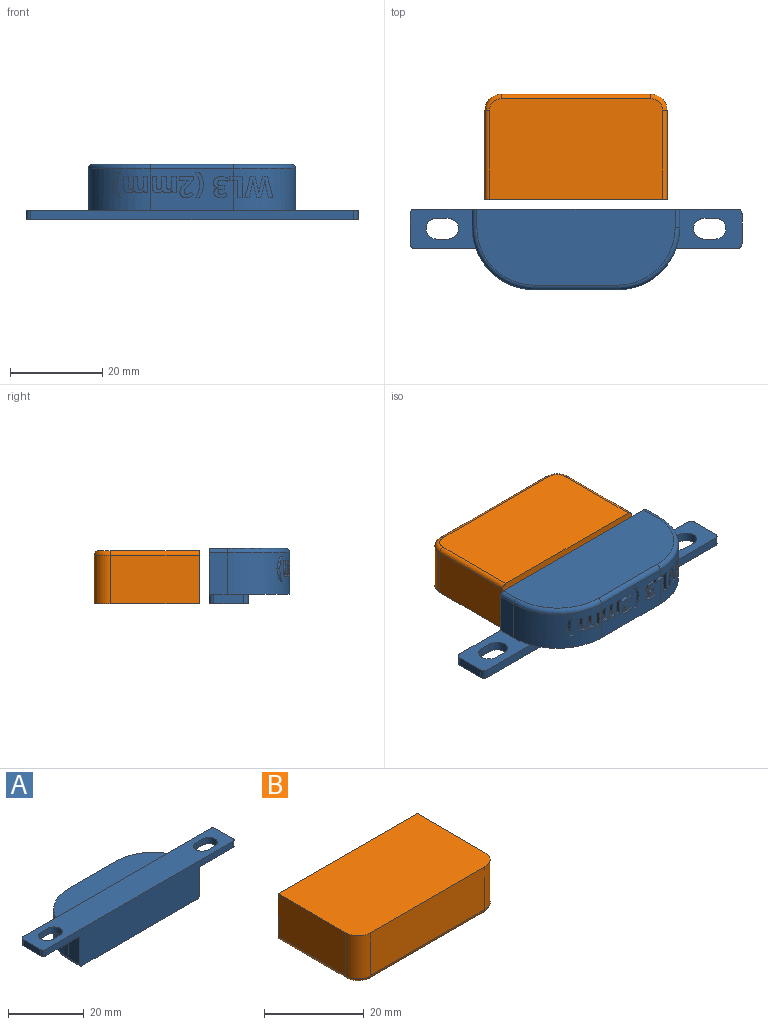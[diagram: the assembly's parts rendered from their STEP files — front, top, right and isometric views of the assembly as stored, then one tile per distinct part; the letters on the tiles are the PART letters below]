
ASSEMBLY  parts=2 mates=1
PART A: 197 faces, bbox 72.1x18.7x12.1 mm
  f0: cylinder r=13.5mm len=13.5mm, axis (0,0,1), area 174mm2, adj f1,f13,f14,f16,f153,f154,f155,f156
  f1: plane 18x9mm, normal (0,1,0), area 130.8mm2, adj f0,f2,f16,f28,f29,f30,f60,f61
  f2: cylinder r=13.5mm len=13.5mm, axis (0,0,1), area 170.5mm2, adj f1,f16,f24,f25,f28,f30,f31,f32
  f3: plane 2.5x2mm, normal (0,1,0), area 5mm2, adj f4,f11,f12,f13
  f4: cylinder r=2.25mm len=4.5mm, axis (0,0,-1), area 14.1mm2, adj f3,f5,f12,f13
  f5: plane 2.5x2mm, normal (0,-1,0), area 5mm2, adj f4,f11,f12,f13
  f6: plane 70x12mm, normal (0,-1,0), area 589.6mm2, adj f10,f12,f13,f14,f15,f22,f24,f25
  f7: plane 70x2mm, normal (0,1,0), area 140mm2, adj f8,f12,f13,f16,f20,f24
  f8: cylinder r=1mm len=2mm, axis (0,0,-1), area 3.1mm2, adj f7,f9,f12,f13
  f9: plane 6.5x2mm, normal (-1,0,0), area 13mm2, adj f8,f10,f12,f13
  f10: cylinder r=1mm len=2mm, axis (0,0,-1), area 3.1mm2, adj f6,f9,f12,f13
  f11: cylinder r=2.25mm len=4.5mm, axis (0,0,-1), area 14.1mm2, adj f3,f5,f12,f13
  f12: plane 72x8.5mm, normal (0,0,1), area 556.8mm2, adj f3,f4,f5,f6,f7,f8,f9,f10
  f13: plane 14.27x8.5mm, normal (0,0,-1), area 88.3mm2, adj f0,f3,f4,f5,f6,f7,f8,f9
  f14: plane 9x4mm, normal (-1,0,0), area 36mm2, adj f0,f6,f13,f192
  f15: plane 43x16.5mm, normal (0,0,-1), area 642.4mm2, adj f6,f192,f193,f194,f195,f196
  f16: plane 43.46x9mm, normal (0,0,1), area 329.1mm2, adj f0,f1,f2,f7
  f17: plane 2.5x2mm, normal (0,1,0), area 5mm2, adj f12,f18,f23,f24
  f18: cylinder r=2.25mm len=4.5mm, axis (0,0,-1), area 14.1mm2, adj f12,f17,f19,f24
  f19: plane 2.5x2mm, normal (0,-1,0), area 5mm2, adj f12,f18,f23,f24
  f20: cylinder r=1mm len=2mm, axis (0,0,-1), area 3.1mm2, adj f7,f12,f21,f24
  f21: plane 6.5x2mm, normal (1,0,0), area 13mm2, adj f12,f20,f22,f24
  f22: cylinder r=1mm len=2mm, axis (0,0,-1), area 3.1mm2, adj f6,f12,f21,f24
  f23: cylinder r=2.25mm len=4.5mm, axis (0,0,-1), area 14.1mm2, adj f12,f17,f19,f24
  f24: plane 14.27x8.5mm, normal (0,0,-1), area 88.3mm2, adj f2,f6,f7,f17,f18,f19,f20,f21
  f25: plane 9x4mm, normal (1,0,0), area 36mm2, adj f2,f6,f24,f196
  f26: cylinder r=13.5mm len=4.47mm, axis (0,0,1), area 5mm2, adj f27,f28,f30,f31,f32,f33
  f27: plane 0.85x0.78mm, normal (0,1,0), area 0.7mm2, adj f26,f28,f29,f30
  f28: plane 2.76x1.14mm, normal (0,0,1), area 2.8mm2, adj f1,f2,f26,f27,f29,f31
  f29: plane 1x0.78mm, normal (1,0,0), area 0.8mm2, adj f1,f27,f28,f30
  f30: plane 1.81x1.03mm, normal (0,0,-1), area 1.8mm2, adj f1,f2,f26,f27,f29,f32
  f31: plane 4.47x1mm, normal (-1,0,0), area 4.5mm2, adj f2,f26,f28,f33
  f32: plane 3.69x1mm, normal (1,0,0), area 3.7mm2, adj f2,f26,f30,f33
  f33: plane 1.1x0.95mm, normal (0,0,-1), area 0.9mm2, adj f2,f26,f31,f32
  f34: cylinder r=13.5mm len=6.05mm, axis (0,0,1), area 15.4mm2, adj f35,f36,f37,f38,f39,f40,f41,f42
  f35: plane 4.49x1.29mm, normal (0.97,0,0.25), area 4.6mm2, adj f2,f34,f36,f56
  f36: plane 1.21x0.93mm, normal (0,0,-1), area 0.9mm2, adj f2,f34,f35,f37
  f37: plane 2.45x1.17mm, normal (-0.97,0,-0.23), area 2.5mm2, adj f2,f34,f36,f38
  f38: extruded ~1.04x0.58mm, area 0.6mm2, adj f2,f34,f37,f39
  f39: extruded ~1.03x0.6mm, area 0.6mm2, adj f2,f34,f38,f40
  f40: extruded ~1.03x0.59mm, area 0.6mm2, adj f2,f34,f39,f41
  f41: extruded ~1.04x0.51mm, area 0.5mm2, adj f2,f34,f40,f42
  f42: plane 2.52x1.26mm, normal (0.97,0,-0.25), area 2.6mm2, adj f2,f34,f41,f43
  f43: plane 1.4x0.9mm, normal (0,0,-1), area 0.9mm2, adj f2,f34,f42,f44
  f44: plane 2.52x1.36mm, normal (-0.97,0,-0.25), area 2.6mm2, adj f2,f34,f43,f45
  f45: extruded ~1.07x0.57mm, area 0.6mm2, adj f2,f34,f44,f46
  f46: extruded ~1.05x0.54mm, area 0.5mm2, adj f2,f34,f45,f47
  f47: extruded ~1.17x1.13mm, area 1.2mm2, adj f2,f34,f46,f48
  f48: plane 2.46x1.39mm, normal (0.97,0,-0.23), area 2.5mm2, adj f2,f34,f47,f49
  f49: plane 1.7x0.93mm, normal (0,0,-1), area 0.9mm2, adj f2,f34,f48,f50
  f50: plane 4.56x1.92mm, normal (-0.97,0,0.25), area 4.6mm2, adj f2,f34,f49,f51
  f51: plane 1.64x1.08mm, normal (0,0,1), area 1.1mm2, adj f2,f34,f50,f52
  f52: plane 2.36x1.31mm, normal (0.97,0,0.25), area 2.4mm2, adj f2,f34,f51,f53
  f53: extruded ~1.05x0.52mm, area 0.5mm2, adj f2,f34,f52,f54
  f54: extruded ~1.04x0.53mm, area 0.5mm2, adj f2,f34,f53,f55
  f55: extruded ~1.04x0.53mm, area 0.5mm2, adj f2,f34,f54,f57
  f56: plane 1.35x1.08mm, normal (0,0,1), area 1.1mm2, adj f2,f34,f35,f58
  f57: extruded ~1.05x0.52mm, area 0.5mm2, adj f2,f34,f55,f58
  f58: plane 2.36x1.25mm, normal (-0.97,0,0.25), area 2.4mm2, adj f2,f34,f56,f57
  f59: plane 5.19x3.48mm, normal (0,1,0), area 11.1mm2, adj f60,f61,f62,f63,f64,f65,f66,f67
  f60: plane 1.72x1mm, normal (1,0,0), area 1.7mm2, adj f1,f59,f61,f85
  f61: extruded ~1x0.78mm, area 0.8mm2, adj f1,f59,f60,f62
  f62: extruded ~1x0.51mm, area 0.6mm2, adj f1,f59,f61,f63
  f63: extruded ~1x0.39mm, area 0.5mm2, adj f1,f59,f62,f64
  f64: extruded ~1x0.55mm, area 0.6mm2, adj f1,f59,f63,f65
  f65: plane 2x1mm, normal (-1,0,0), area 2mm2, adj f1,f59,f64,f66
  f66: plane 1x0.94mm, normal (0,0,1), area 0.9mm2, adj f1,f59,f65,f67
  f67: plane 2.23x1mm, normal (1,0,0), area 2.2mm2, adj f1,f59,f66,f68
  f68: extruded ~1x0.96mm, area 1mm2, adj f1,f59,f67,f69
  f69: extruded ~1x0.88mm, area 1mm2, adj f1,f59,f68,f70
  f70: extruded ~1x0.6mm, area 0.6mm2, adj f1,f59,f69,f71
  f71: extruded ~1x0.41mm, area 0.6mm2, adj f1,f59,f70,f72
  f72: plane 1x0.08mm, normal (0,0,-1), area 0.1mm2, adj f1,f59,f71,f73
  f73: extruded ~1.04x1mm, area 1.2mm2, adj f1,f59,f72,f74
  f74: extruded ~1x0.6mm, area 0.6mm2, adj f1,f59,f73,f75
  f75: extruded ~1x0.4mm, area 0.5mm2, adj f1,f59,f74,f76
  f76: plane 1x0.05mm, normal (0,0,-1), area 0.1mm2, adj f1,f59,f75,f77
  f77: plane 1x0.44mm, normal (0.96,0,-0.28), area 0.5mm2, adj f1,f59,f76,f78
  f78: plane 1x0.71mm, normal (0,0,-1), area 0.7mm2, adj f1,f59,f77,f79
  f79: plane 3.42x1mm, normal (-1,0,0), area 3.4mm2, adj f1,f59,f78,f80
  f80: plane 1x0.93mm, normal (0,0,1), area 0.9mm2, adj f1,f59,f79,f81
  f81: plane 1.61x1mm, normal (1,0,0), area 1.6mm2, adj f1,f59,f80,f82
  f82: extruded ~1x0.87mm, area 0.9mm2, adj f1,f59,f81,f83
  f83: extruded ~1x0.52mm, area 0.6mm2, adj f1,f59,f82,f84
  f84: extruded ~1x0.39mm, area 0.5mm2, adj f1,f59,f83,f86
  f85: plane 1x0.93mm, normal (0,0,1), area 0.9mm2, adj f1,f59,f60,f87
  f86: extruded ~1x0.55mm, area 0.6mm2, adj f1,f59,f84,f87
  f87: plane 2x1mm, normal (-1,0,0), area 2mm2, adj f1,f59,f85,f86
  f88: plane 4.53x3.14mm, normal (0,1,0), area 7.4mm2, adj f89,f90,f91,f92,f93,f94,f95,f96
  f89: plane 1x0.8mm, normal (1,0,0), area 0.8mm2, adj f1,f88,f90,f110
  f90: plane 1.95x1mm, normal (0,0,-1), area 1.9mm2, adj f1,f88,f89,f91
  f91: plane 1x0.04mm, normal (1,0,0), area 0mm2, adj f1,f88,f90,f92
  f92: plane 1x0.58mm, normal (0.69,0,0.73), area 0.8mm2, adj f1,f88,f91,f93
  f93: extruded ~1x0.81mm, area 1.1mm2, adj f1,f88,f92,f94
  f94: extruded ~1x0.55mm, area 0.7mm2, adj f1,f88,f93,f95
  f95: extruded ~1x0.58mm, area 0.6mm2, adj f1,f88,f94,f96
  f96: extruded ~1x0.63mm, area 0.7mm2, adj f1,f88,f95,f97
  f97: extruded ~1x0.5mm, area 0.7mm2, adj f1,f88,f96,f98
  f98: extruded ~1x0.74mm, area 0.8mm2, adj f1,f88,f97,f99
  f99: extruded ~1x0.58mm, area 0.6mm2, adj f1,f88,f98,f100
  f100: extruded ~1x0.47mm, area 0.5mm2, adj f1,f88,f99,f101
  f101: extruded ~1x0.55mm, area 0.7mm2, adj f1,f88,f100,f102
  f102: plane 1x0.61mm, normal (-0.76,0,0.65), area 0.8mm2, adj f1,f88,f101,f103
  f103: extruded ~1x0.51mm, area 0.6mm2, adj f1,f88,f102,f104
  f104: extruded ~1x0.5mm, area 0.5mm2, adj f1,f88,f103,f105
  f105: extruded ~1x0.4mm, area 0.4mm2, adj f1,f88,f104,f106
  f106: extruded ~1x0.4mm, area 0.4mm2, adj f1,f88,f105,f107
  f107: extruded ~1x0.35mm, area 0.4mm2, adj f1,f88,f106,f108
  f108: extruded ~1x0.37mm, area 0.4mm2, adj f1,f88,f107,f109
  f109: extruded ~1x0.71mm, area 1mm2, adj f1,f88,f108,f111
  f110: plane 3.13x1mm, normal (0,0,1), area 3.1mm2, adj f1,f88,f89,f112
  f111: plane 1.13x1.12mm, normal (-0.71,0,-0.7), area 1.6mm2, adj f1,f88,f109,f112
  f112: plane 1x0.66mm, normal (-1,0,0), area 0.7mm2, adj f1,f88,f110,f111
  f113: plane 5.46x1.69mm, normal (0,1,0), area 4.4mm2, adj f114,f115,f116,f117,f118,f119,f120,f121
  f114: extruded ~1.49x1mm, area 1.5mm2, adj f1,f113,f115,f121
  f115: extruded ~1.21x1mm, area 1.4mm2, adj f1,f113,f114,f116
  f116: plane 1x0.76mm, normal (0,0,1), area 0.8mm2, adj f1,f113,f115,f117
  f117: extruded ~1.27x1mm, area 1.4mm2, adj f1,f113,f116,f118
  f118: extruded ~1.45x1mm, area 1.5mm2, adj f1,f113,f117,f119
  f119: extruded ~1.45x1mm, area 1.5mm2, adj f1,f113,f118,f120
  f120: extruded ~1.3x1mm, area 1.5mm2, adj f1,f113,f119,f122
  f121: extruded ~1.52x1mm, area 1.5mm2, adj f1,f113,f114,f123
  f122: plane 1x0.76mm, normal (0,0,-1), area 0.8mm2, adj f1,f113,f120,f123
  f123: extruded ~1.24x1mm, area 1.4mm2, adj f1,f113,f121,f122
  f124: plane 4.6x3.09mm, normal (0,1,0), area 7.6mm2, adj f125,f126,f127,f128,f129,f130,f131,f132
  f125: extruded ~1x0.78mm, area 0.9mm2, adj f1,f124,f126,f149
  f126: extruded ~1.1x1mm, area 1.1mm2, adj f1,f124,f125,f127
  f127: extruded ~1.46x1mm, area 1.5mm2, adj f1,f124,f126,f128
  f128: plane 1x0.65mm, normal (-0.83,0,0.56), area 0.8mm2, adj f1,f124,f127,f129
  f129: extruded ~1x0.51mm, area 0.6mm2, adj f1,f124,f128,f130
  f130: extruded ~1x0.45mm, area 0.5mm2, adj f1,f124,f129,f131
  f131: extruded ~1x0.64mm, area 0.9mm2, adj f1,f124,f130,f132
  f132: extruded ~1x0.47mm, area 0.6mm2, adj f1,f124,f131,f133
  f133: extruded ~1x0.76mm, area 0.8mm2, adj f1,f124,f132,f134
  f134: plane 1x0.35mm, normal (0,0,-1), area 0.3mm2, adj f1,f124,f133,f135
  f135: plane 1x0.73mm, normal (-1,0,0), area 0.7mm2, adj f1,f124,f134,f136
  f136: plane 1x0.34mm, normal (0,0,1), area 0.3mm2, adj f1,f124,f135,f137
  f137: extruded ~1x0.82mm, area 0.8mm2, adj f1,f124,f136,f138
  f138: extruded ~1x0.45mm, area 0.5mm2, adj f1,f124,f137,f139
  f139: extruded ~1x0.51mm, area 0.6mm2, adj f1,f124,f138,f140
  f140: extruded ~1x0.69mm, area 0.7mm2, adj f1,f124,f139,f141
  f141: extruded ~1x0.62mm, area 0.6mm2, adj f1,f124,f140,f142
  f142: extruded ~1x0.57mm, area 0.6mm2, adj f1,f124,f141,f143
  f143: plane 1x0.8mm, normal (-1,0,0), area 0.8mm2, adj f1,f124,f142,f144
  f144: extruded ~1.29x1mm, area 1.3mm2, adj f1,f124,f143,f145
  f145: extruded ~1.34x1mm, area 1.4mm2, adj f1,f124,f144,f146
  f146: extruded ~1x1mm, area 1.2mm2, adj f1,f124,f145,f147
  f147: extruded ~1x0.71mm, area 0.8mm2, adj f1,f124,f146,f148
  f148: extruded ~1x0.82mm, area 0.9mm2, adj f1,f124,f147,f150
  f149: extruded ~1x0.71mm, area 0.8mm2, adj f1,f124,f125,f151
  f150: plane 1x0.02mm, normal (1,0,0), area 0mm2, adj f1,f124,f148,f151
  f151: extruded ~1x0.71mm, area 0.8mm2, adj f1,f124,f149,f150
  f152: cylinder r=13.5mm len=5.46mm, axis (0,0,1), area 5.3mm2, adj f153,f154,f155,f156,f157,f158,f159,f160
  f153: extruded ~1.51x1.17mm, area 1.5mm2, adj f0,f152,f154,f160
  f154: extruded ~1.46x1.24mm, area 1.4mm2, adj f0,f152,f153,f155
  f155: plane 1.45x0.76mm, normal (0,0,-1), area 0.8mm2, adj f0,f152,f154,f156
  f156: extruded ~1.38x1.3mm, area 1.5mm2, adj f0,f152,f155,f157
  f157: extruded ~1.45x1.14mm, area 1.5mm2, adj f0,f152,f156,f158
  f158: extruded ~1.45x1.14mm, area 1.5mm2, adj f0,f152,f157,f159
  f159: extruded ~1.37x1.26mm, area 1.4mm2, adj f0,f152,f158,f161
  f160: extruded ~1.5x1.18mm, area 1.5mm2, adj f0,f152,f153,f162
  f161: plane 1.45x0.76mm, normal (0,0,1), area 0.8mm2, adj f0,f152,f159,f162
  f162: extruded ~1.46x1.21mm, area 1.4mm2, adj f0,f152,f160,f161
  f163: cylinder r=13.5mm len=5.19mm, axis (0,0,1), area 11.5mm2, adj f164,f165,f166,f167,f168,f169,f170,f171
  f164: plane 1.72x1mm, normal (1,0,0), area 1.7mm2, adj f0,f163,f165,f189
  f165: extruded ~1.05x0.78mm, area 0.8mm2, adj f0,f163,f164,f166
  f166: extruded ~1.16x0.51mm, area 0.6mm2, adj f0,f163,f165,f167
  f167: extruded ~1.14x0.39mm, area 0.5mm2, adj f0,f163,f166,f168
  f168: extruded ~1.05x0.55mm, area 0.6mm2, adj f0,f163,f167,f169
  f169: plane 2x1mm, normal (-1,0,0), area 2mm2, adj f0,f163,f168,f170
  f170: plane 1.4x0.94mm, normal (0,0,1), area 0.9mm2, adj f0,f163,f169,f171
  f171: plane 2.23x1mm, normal (1,0,0), area 2.2mm2, adj f0,f163,f170,f172
  f172: extruded ~1.14x0.96mm, area 1mm2, adj f0,f163,f171,f173
  f173: extruded ~1.36x0.88mm, area 1mm2, adj f0,f163,f172,f174
  f174: extruded ~1.2x0.6mm, area 0.6mm2, adj f0,f163,f173,f175
  f175: extruded ~1.12x0.41mm, area 0.6mm2, adj f0,f163,f174,f176
  f176: plane 1.02x0.08mm, normal (0,0,-1), area 0.1mm2, adj f0,f163,f175,f177
  f177: extruded ~1.24x1.04mm, area 1.2mm2, adj f0,f163,f176,f178
  f178: extruded ~1.1x0.6mm, area 0.6mm2, adj f0,f163,f177,f179
  f179: extruded ~1.05x0.4mm, area 0.5mm2, adj f0,f163,f178,f180
  f180: plane 1.01x0.05mm, normal (0,0,-1), area 0.1mm2, adj f0,f163,f179,f181
  f181: plane 1.01x0.44mm, normal (0.96,0,-0.28), area 0.5mm2, adj f0,f163,f180,f182
  f182: plane 1.05x0.71mm, normal (0,0,-1), area 0.7mm2, adj f0,f163,f181,f183
  f183: plane 3.42x1mm, normal (-1,0,0), area 3.4mm2, adj f0,f163,f182,f184
  f184: plane 1.07x0.93mm, normal (0,0,1), area 0.9mm2, adj f0,f163,f183,f185
  f185: plane 1.61x1mm, normal (1,0,0), area 1.6mm2, adj f0,f163,f184,f186
  f186: extruded ~1.02x0.87mm, area 0.9mm2, adj f0,f163,f185,f187
  f187: extruded ~1.08x0.52mm, area 0.6mm2, adj f0,f163,f186,f188
  f188: extruded ~1.07x0.39mm, area 0.5mm2, adj f0,f163,f187,f190
  f189: plane 1.23x0.93mm, normal (0,0,1), area 0.9mm2, adj f0,f163,f164,f191
  f190: extruded ~1.03x0.55mm, area 0.6mm2, adj f0,f163,f188,f191
  f191: plane 2x1mm, normal (-1,0,0), area 2mm2, adj f0,f163,f189,f190
  f192: cylinder r=1mm len=4mm, axis (0,1,0), area 6.3mm2, adj f6,f14,f15,f193
  f193: torus R=12.5mm, axis (0,0,1), area 32.4mm2, adj f0,f15,f192,f194
  f194: cylinder r=1mm len=18mm, axis (1,0,0), area 28.3mm2, adj f1,f15,f193,f195
  f195: torus R=12.5mm, axis (0,0,1), area 32.4mm2, adj f2,f15,f194,f196
  f196: cylinder r=1mm len=4mm, axis (0,1,0), area 6.3mm2, adj f6,f15,f25,f195
PART B: 178 faces, bbox 40.1x23.1x11.5 mm
  f0: plane 39.5x11.5mm, normal (0,1,0), area 388.3mm2, adj f2,f4,f5,f6,f8,f9,f10,f11
  f1: plane 32.5x10.5mm, normal (0,-1,0), area 341.3mm2, adj f3,f5,f7,f175
  f2: plane 19.3x10.5mm, normal (-1,0,0), area 202.7mm2, adj f0,f3,f5,f173
  f3: cylinder r=3.5mm len=10.5mm, axis (0,0,1), area 57.7mm2, adj f1,f2,f5,f174
  f4: plane 37.5x21.8mm, normal (0,0,-1), area 814.8mm2, adj f0,f173,f174,f175,f176,f177
  f5: plane 39.5x22.8mm, normal (0,0,1), area 895.3mm2, adj f0,f1,f2,f3,f6,f7
  f6: plane 19.3x10.5mm, normal (1,0,0), area 202.7mm2, adj f0,f5,f7,f177
  f7: cylinder r=3.5mm len=10.5mm, axis (0,0,1), area 57.7mm2, adj f1,f5,f6,f176
  f8: extruded ~1.5x1mm, area 1.5mm2, adj f0,f9,f17,f18
  f9: extruded ~1.51x1mm, area 1.5mm2, adj f0,f8,f10,f18
  f10: extruded ~1.24x1mm, area 1.4mm2, adj f0,f9,f11,f18
  f11: plane 1x0.76mm, normal (0,0,-1), area 0.8mm2, adj f0,f10,f12,f18
  f12: extruded ~1.3x1mm, area 1.5mm2, adj f0,f11,f13,f18
  f13: extruded ~1.45x1mm, area 1.5mm2, adj f0,f12,f14,f18
  f14: extruded ~1.45x1mm, area 1.5mm2, adj f0,f13,f15,f18
  f15: extruded ~1.26x1mm, area 1.4mm2, adj f0,f14,f16,f18
  f16: plane 1x0.76mm, normal (0,0,1), area 0.8mm2, adj f0,f15,f17,f18
  f17: extruded ~1.21x1mm, area 1.4mm2, adj f0,f8,f16,f18
  f18: plane 5.46x1.69mm, normal (0,1,0), area 4.4mm2, adj f8,f9,f10,f11,f12,f13,f14,f15
  f19: plane 1x0.93mm, normal (0,0,1), area 0.9mm2, adj f0,f20,f46,f47
  f20: plane 1.72x1mm, normal (1,0,0), area 1.7mm2, adj f0,f19,f21,f47
  f21: extruded ~1x0.78mm, area 0.8mm2, adj f0,f20,f22,f47
  f22: extruded ~1x0.51mm, area 0.6mm2, adj f0,f21,f23,f47
  f23: extruded ~1x0.39mm, area 0.5mm2, adj f0,f22,f24,f47
  f24: extruded ~1x0.55mm, area 0.6mm2, adj f0,f23,f25,f47
  f25: plane 2x1mm, normal (-1,0,0), area 2mm2, adj f0,f24,f26,f47
  f26: plane 1x0.94mm, normal (0,0,1), area 0.9mm2, adj f0,f25,f27,f47
  f27: plane 2.23x1mm, normal (1,0,0), area 2.2mm2, adj f0,f26,f28,f47
  f28: extruded ~1x0.96mm, area 1mm2, adj f0,f27,f29,f47
  f29: extruded ~1x0.88mm, area 1mm2, adj f0,f28,f30,f47
  f30: extruded ~1x0.6mm, area 0.6mm2, adj f0,f29,f31,f47
  f31: extruded ~1x0.41mm, area 0.6mm2, adj f0,f30,f32,f47
  f32: plane 1x0.08mm, normal (0,0,-1), area 0.1mm2, adj f0,f31,f33,f47
  f33: extruded ~1.04x1mm, area 1.2mm2, adj f0,f32,f34,f47
  f34: extruded ~1x0.6mm, area 0.6mm2, adj f0,f33,f35,f47
  f35: extruded ~1x0.4mm, area 0.5mm2, adj f0,f34,f36,f47
  f36: plane 1x0.05mm, normal (0,0,-1), area 0.1mm2, adj f0,f35,f37,f47
  f37: plane 1x0.44mm, normal (0.96,0,-0.28), area 0.5mm2, adj f0,f36,f38,f47
  f38: plane 1x0.71mm, normal (0,0,-1), area 0.7mm2, adj f0,f37,f39,f47
  f39: plane 3.42x1mm, normal (-1,0,0), area 3.4mm2, adj f0,f38,f40,f47
  f40: plane 1x0.93mm, normal (0,0,1), area 0.9mm2, adj f0,f39,f41,f47
  f41: plane 1.61x1mm, normal (1,0,0), area 1.6mm2, adj f0,f40,f42,f47
  f42: extruded ~1x0.87mm, area 0.9mm2, adj f0,f41,f43,f47
  f43: extruded ~1x0.52mm, area 0.6mm2, adj f0,f42,f44,f47
  f44: extruded ~1x0.39mm, area 0.5mm2, adj f0,f43,f45,f47
  f45: extruded ~1x0.55mm, area 0.6mm2, adj f0,f44,f46,f47
  f46: plane 2x1mm, normal (-1,0,0), area 2mm2, adj f0,f19,f45,f47
  f47: plane 5.19x3.48mm, normal (0,1,0), area 11.1mm2, adj f19,f20,f21,f22,f23,f24,f25,f26
  f48: plane 1x0.93mm, normal (0,0,1), area 0.9mm2, adj f0,f49,f75,f76
  f49: plane 1.72x1mm, normal (1,0,0), area 1.7mm2, adj f0,f48,f50,f76
  f50: extruded ~1x0.78mm, area 0.8mm2, adj f0,f49,f51,f76
  f51: extruded ~1x0.51mm, area 0.6mm2, adj f0,f50,f52,f76
  f52: extruded ~1x0.39mm, area 0.5mm2, adj f0,f51,f53,f76
  f53: extruded ~1x0.55mm, area 0.6mm2, adj f0,f52,f54,f76
  f54: plane 2x1mm, normal (-1,0,0), area 2mm2, adj f0,f53,f55,f76
  f55: plane 1x0.94mm, normal (0,0,1), area 0.9mm2, adj f0,f54,f56,f76
  f56: plane 2.23x1mm, normal (1,0,0), area 2.2mm2, adj f0,f55,f57,f76
  f57: extruded ~1x0.96mm, area 1mm2, adj f0,f56,f58,f76
  f58: extruded ~1x0.88mm, area 1mm2, adj f0,f57,f59,f76
  f59: extruded ~1x0.6mm, area 0.6mm2, adj f0,f58,f60,f76
  f60: extruded ~1x0.41mm, area 0.6mm2, adj f0,f59,f61,f76
  f61: plane 1x0.08mm, normal (0,0,-1), area 0.1mm2, adj f0,f60,f62,f76
  f62: extruded ~1.04x1mm, area 1.2mm2, adj f0,f61,f63,f76
  f63: extruded ~1x0.6mm, area 0.6mm2, adj f0,f62,f64,f76
  f64: extruded ~1x0.4mm, area 0.5mm2, adj f0,f63,f65,f76
  f65: plane 1x0.05mm, normal (0,0,-1), area 0.1mm2, adj f0,f64,f66,f76
  f66: plane 1x0.44mm, normal (0.96,0,-0.28), area 0.5mm2, adj f0,f65,f67,f76
  f67: plane 1x0.71mm, normal (0,0,-1), area 0.7mm2, adj f0,f66,f68,f76
  f68: plane 3.42x1mm, normal (-1,0,0), area 3.4mm2, adj f0,f67,f69,f76
  f69: plane 1x0.93mm, normal (0,0,1), area 0.9mm2, adj f0,f68,f70,f76
  f70: plane 1.61x1mm, normal (1,0,0), area 1.6mm2, adj f0,f69,f71,f76
  f71: extruded ~1x0.87mm, area 0.9mm2, adj f0,f70,f72,f76
  f72: extruded ~1x0.52mm, area 0.6mm2, adj f0,f71,f73,f76
  f73: extruded ~1x0.39mm, area 0.5mm2, adj f0,f72,f74,f76
  f74: extruded ~1x0.55mm, area 0.6mm2, adj f0,f73,f75,f76
  f75: plane 2x1mm, normal (-1,0,0), area 2mm2, adj f0,f48,f74,f76
  f76: plane 5.19x3.48mm, normal (0,1,0), area 11.1mm2, adj f48,f49,f50,f51,f52,f53,f54,f55
  f77: plane 3.13x1mm, normal (0,0,1), area 3.1mm2, adj f0,f78,f100,f101
  f78: plane 1x0.8mm, normal (1,0,0), area 0.8mm2, adj f0,f77,f79,f101
  f79: plane 1.95x1mm, normal (0,0,-1), area 1.9mm2, adj f0,f78,f80,f101
  f80: plane 1x0.04mm, normal (1,0,0), area 0mm2, adj f0,f79,f81,f101
  f81: plane 1x0.58mm, normal (0.69,0,0.73), area 0.8mm2, adj f0,f80,f82,f101
  f82: extruded ~1x0.81mm, area 1.1mm2, adj f0,f81,f83,f101
  f83: extruded ~1x0.55mm, area 0.7mm2, adj f0,f82,f84,f101
  f84: extruded ~1x0.58mm, area 0.6mm2, adj f0,f83,f85,f101
  f85: extruded ~1x0.63mm, area 0.7mm2, adj f0,f84,f86,f101
  f86: extruded ~1x0.5mm, area 0.7mm2, adj f0,f85,f87,f101
  f87: extruded ~1x0.74mm, area 0.8mm2, adj f0,f86,f88,f101
  f88: extruded ~1x0.58mm, area 0.6mm2, adj f0,f87,f89,f101
  f89: extruded ~1x0.47mm, area 0.5mm2, adj f0,f88,f90,f101
  f90: extruded ~1x0.55mm, area 0.7mm2, adj f0,f89,f91,f101
  f91: plane 1x0.61mm, normal (-0.76,0,0.65), area 0.8mm2, adj f0,f90,f92,f101
  f92: extruded ~1x0.51mm, area 0.6mm2, adj f0,f91,f93,f101
  f93: extruded ~1x0.5mm, area 0.5mm2, adj f0,f92,f94,f101
  f94: extruded ~1x0.4mm, area 0.4mm2, adj f0,f93,f95,f101
  f95: extruded ~1x0.4mm, area 0.4mm2, adj f0,f94,f96,f101
  f96: extruded ~1x0.35mm, area 0.4mm2, adj f0,f95,f97,f101
  f97: extruded ~1x0.37mm, area 0.4mm2, adj f0,f96,f98,f101
  f98: extruded ~1x0.71mm, area 1mm2, adj f0,f97,f99,f101
  f99: plane 1.13x1.12mm, normal (-0.71,0,-0.7), area 1.6mm2, adj f0,f98,f100,f101
  f100: plane 1x0.66mm, normal (-1,0,0), area 0.7mm2, adj f0,f77,f99,f101
  f101: plane 4.53x3.14mm, normal (0,1,0), area 7.4mm2, adj f77,f78,f79,f80,f81,f82,f83,f84
  f102: extruded ~1.52x1mm, area 1.5mm2, adj f0,f103,f111,f112
  f103: extruded ~1.49x1mm, area 1.5mm2, adj f0,f102,f104,f112
  f104: extruded ~1.21x1mm, area 1.4mm2, adj f0,f103,f105,f112
  f105: plane 1x0.76mm, normal (0,0,1), area 0.8mm2, adj f0,f104,f106,f112
  f106: extruded ~1.27x1mm, area 1.4mm2, adj f0,f105,f107,f112
  f107: extruded ~1.45x1mm, area 1.5mm2, adj f0,f106,f108,f112
  f108: extruded ~1.45x1mm, area 1.5mm2, adj f0,f107,f109,f112
  f109: extruded ~1.3x1mm, area 1.5mm2, adj f0,f108,f110,f112
  f110: plane 1x0.76mm, normal (0,0,-1), area 0.8mm2, adj f0,f109,f111,f112
  f111: extruded ~1.24x1mm, area 1.4mm2, adj f0,f102,f110,f112
  f112: plane 5.46x1.69mm, normal (0,1,0), area 4.4mm2, adj f102,f103,f104,f105,f106,f107,f108,f109
  f113: extruded ~1x0.71mm, area 0.8mm2, adj f0,f114,f139,f140
  f114: extruded ~1x0.78mm, area 0.9mm2, adj f0,f113,f115,f140
  f115: extruded ~1.1x1mm, area 1.1mm2, adj f0,f114,f116,f140
  f116: extruded ~1.46x1mm, area 1.5mm2, adj f0,f115,f117,f140
  f117: plane 1x0.65mm, normal (-0.83,0,0.56), area 0.8mm2, adj f0,f116,f118,f140
  f118: extruded ~1x0.51mm, area 0.6mm2, adj f0,f117,f119,f140
  f119: extruded ~1x0.45mm, area 0.5mm2, adj f0,f118,f120,f140
  f120: extruded ~1x0.64mm, area 0.9mm2, adj f0,f119,f121,f140
  f121: extruded ~1x0.47mm, area 0.6mm2, adj f0,f120,f122,f140
  f122: extruded ~1x0.76mm, area 0.8mm2, adj f0,f121,f123,f140
  f123: plane 1x0.35mm, normal (0,0,-1), area 0.3mm2, adj f0,f122,f124,f140
  f124: plane 1x0.73mm, normal (-1,0,0), area 0.7mm2, adj f0,f123,f125,f140
  f125: plane 1x0.34mm, normal (0,0,1), area 0.3mm2, adj f0,f124,f126,f140
  f126: extruded ~1x0.82mm, area 0.8mm2, adj f0,f125,f127,f140
  f127: extruded ~1x0.45mm, area 0.5mm2, adj f0,f126,f128,f140
  f128: extruded ~1x0.51mm, area 0.6mm2, adj f0,f127,f129,f140
  f129: extruded ~1x0.69mm, area 0.7mm2, adj f0,f128,f130,f140
  f130: extruded ~1x0.62mm, area 0.6mm2, adj f0,f129,f131,f140
  f131: extruded ~1x0.57mm, area 0.6mm2, adj f0,f130,f132,f140
  f132: plane 1x0.8mm, normal (-1,0,0), area 0.8mm2, adj f0,f131,f133,f140
  f133: extruded ~1.29x1mm, area 1.3mm2, adj f0,f132,f134,f140
  f134: extruded ~1.34x1mm, area 1.4mm2, adj f0,f133,f135,f140
  f135: extruded ~1x1mm, area 1.2mm2, adj f0,f134,f136,f140
  f136: extruded ~1x0.71mm, area 0.8mm2, adj f0,f135,f137,f140
  f137: extruded ~1x0.82mm, area 0.9mm2, adj f0,f136,f138,f140
  f138: plane 1x0.02mm, normal (1,0,0), area 0mm2, adj f0,f137,f139,f140
  f139: extruded ~1x0.71mm, area 0.8mm2, adj f0,f113,f138,f140
  f140: plane 4.6x3.09mm, normal (0,1,0), area 7.6mm2, adj f113,f114,f115,f116,f117,f118,f119,f120
  f141: plane 4.47x1mm, normal (-1,0,0), area 4.5mm2, adj f0,f142,f146,f147
  f142: plane 2.76x1mm, normal (0,0,1), area 2.8mm2, adj f0,f141,f143,f147
  f143: plane 1x0.78mm, normal (1,0,0), area 0.8mm2, adj f0,f142,f144,f147
  f144: plane 1.81x1mm, normal (0,0,-1), area 1.8mm2, adj f0,f143,f145,f147
  f145: plane 3.69x1mm, normal (1,0,0), area 3.7mm2, adj f0,f144,f146,f147
  f146: plane 1x0.95mm, normal (0,0,-1), area 0.9mm2, adj f0,f141,f145,f147
  f147: plane 4.47x2.76mm, normal (0,1,0), area 5.7mm2, adj f141,f142,f143,f144,f145,f146
  f148: plane 1.08x1mm, normal (0,0,1), area 1.1mm2, adj f0,f149,f171,f172
  f149: plane 4.47x1.14mm, normal (0.97,0,0.25), area 4.6mm2, adj f0,f148,f150,f172
  f150: plane 1x0.93mm, normal (0,0,-1), area 0.9mm2, adj f0,f149,f151,f172
  f151: plane 2.44x1mm, normal (-0.97,0,-0.23), area 2.5mm2, adj f0,f150,f152,f172
  f152: extruded ~1x0.58mm, area 0.6mm2, adj f0,f151,f153,f172
  f153: extruded ~1x0.6mm, area 0.6mm2, adj f0,f152,f154,f172
  f154: extruded ~1x0.59mm, area 0.6mm2, adj f0,f153,f155,f172
  f155: extruded ~1x0.51mm, area 0.5mm2, adj f0,f154,f156,f172
  f156: plane 2.51x1mm, normal (0.97,0,-0.25), area 2.6mm2, adj f0,f155,f157,f172
  f157: plane 1x0.9mm, normal (0,0,-1), area 0.9mm2, adj f0,f156,f158,f172
  f158: plane 2.51x1mm, normal (-0.97,0,-0.25), area 2.6mm2, adj f0,f157,f159,f172
  f159: extruded ~1x0.57mm, area 0.6mm2, adj f0,f158,f160,f172
  f160: extruded ~1x0.54mm, area 0.5mm2, adj f0,f159,f161,f172
  f161: extruded ~1.17x1mm, area 1.2mm2, adj f0,f160,f162,f172
  f162: plane 2.44x1mm, normal (0.97,0,-0.23), area 2.5mm2, adj f0,f161,f163,f172
  f163: plane 1x0.93mm, normal (0,0,-1), area 0.9mm2, adj f0,f162,f164,f172
  f164: plane 4.47x1.14mm, normal (-0.97,0,0.25), area 4.6mm2, adj f0,f163,f165,f172
  f165: plane 1.08x1mm, normal (0,0,1), area 1.1mm2, adj f0,f164,f166,f172
  f166: plane 2.34x1mm, normal (0.97,0,0.25), area 2.4mm2, adj f0,f165,f167,f172
  f167: extruded ~1x0.52mm, area 0.5mm2, adj f0,f166,f168,f172
  f168: extruded ~1x0.53mm, area 0.5mm2, adj f0,f167,f169,f172
  f169: extruded ~1x0.53mm, area 0.5mm2, adj f0,f168,f170,f172
  f170: extruded ~1x0.52mm, area 0.5mm2, adj f0,f169,f171,f172
  f171: plane 2.35x1mm, normal (-0.97,0,0.25), area 2.4mm2, adj f0,f148,f170,f172
  f172: plane 6.05x4.47mm, normal (0,1,0), area 13.8mm2, adj f148,f149,f150,f151,f152,f153,f154,f155
  f173: cylinder r=1mm len=19.3mm, axis (0,1,0), area 30.3mm2, adj f0,f2,f4,f174
  f174: torus R=2.5mm, axis (0,0,1), area 7.7mm2, adj f3,f4,f173,f175
  f175: cylinder r=1mm len=32.5mm, axis (-1,0,0), area 51.1mm2, adj f1,f4,f174,f176
  f176: torus R=2.5mm, axis (0,0,1), area 7.7mm2, adj f4,f7,f175,f177
  f177: cylinder r=1mm len=19.3mm, axis (0,1,0), area 30.3mm2, adj f0,f4,f6,f176
PLACE A rot(axis=(1,0,0),180deg) t=(0.59,6.62,3)mm fixed
PLACE B rot(axis=(1,0,0),180deg) t=(0.59,3.72,1)mm
MATE planar A.f12 <-> B.f5  axis (0,0,-1) through (0.59,2.37,1)mm
